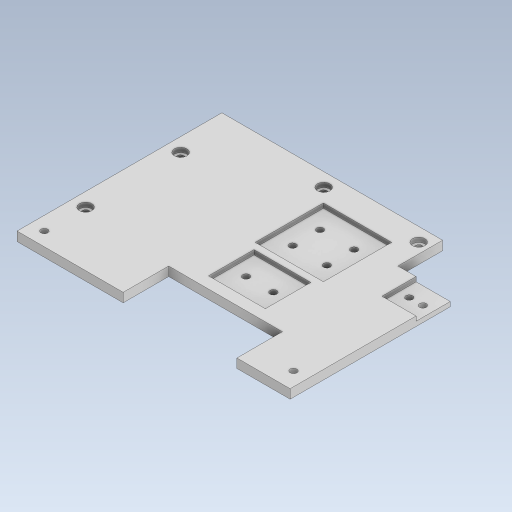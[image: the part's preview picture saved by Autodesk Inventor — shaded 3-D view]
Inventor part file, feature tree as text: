
AUTODESK INVENTOR PART (.ipt)
format: ipt  version: 2023.5 (Build 275446000, 446)  size: 383,488 bytes
history: native  units: in
note: dims shown in document units (in); Inventor stores cm internally (conversion verified against a paired STEP export)
features: extrude x2, sketch x1
ambient origin geometry x8: Origin, YZ Plane, XZ Plane, XY Plane, X Axis, Y Axis, Z Axis, Center Point
bodies: Solid1 (feature_tree)
feature tree (3):
  sketch  "Sketch1"  dims[d28=0.1575in d29=0.0in d30=0.0787in d31=0.0in d32=0.2953in d33=0.4724in d34=0.4724in d35=0.2953in d36=0.0in d37=0.0in d39=0.315in d40=0.2165in d41=0.2165in d42=0.2165in d43=0.2165in]
  extrude  "Extrusion1"  Depth=0.0787in TaperAngle=0.0deg
  extrude  "Extrusion2"  Depth=0.315in
